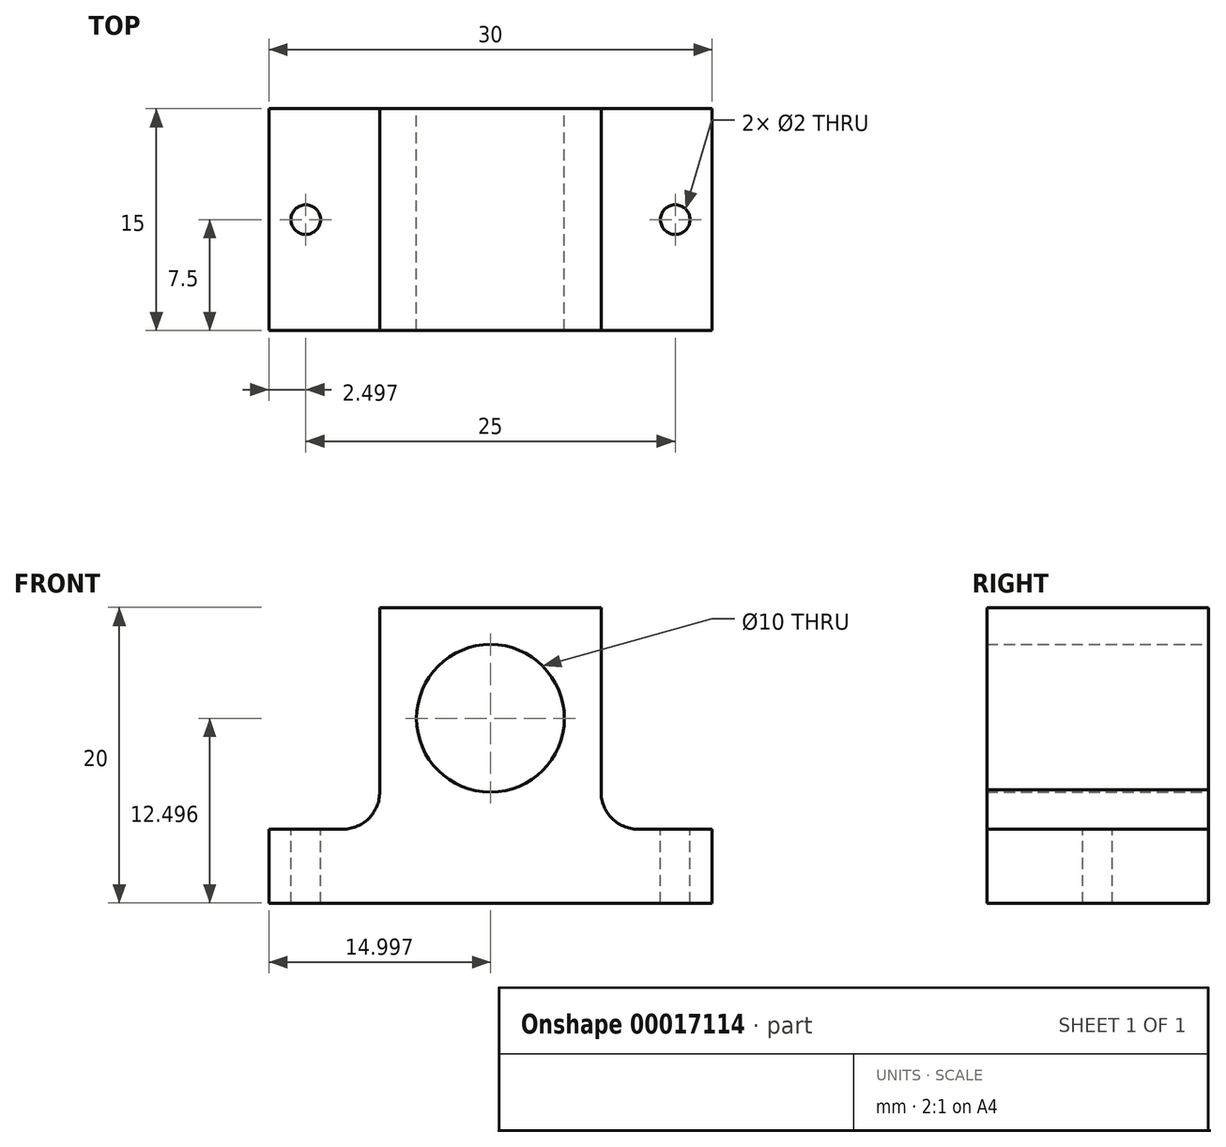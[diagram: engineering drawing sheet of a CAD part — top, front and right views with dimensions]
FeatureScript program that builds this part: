
annotation { "Feature Type Name" : "Feature", "Feature Type Description" : "" }
export const myFeature = defineFeature(function(context is Context, id is Id, definition is map)
    precondition{}
    {
        {
            var Q0;
            Q0=qCreatedBy(makeId("Front.planeOp"),FACE);
            var sketch = newSketch(context, id + "F0", { "sketchPlane" : qUnion([Q0])});
            skLineSegment(sketch, "E0.top", {"start": v(-46.25, -41.24) * mm, "end": v(-16.25, -41.24) * mm});
            skLineSegment(sketch, "E1", {"start": v(-46.25, -36.24) * mm, "end": v(-41.25, -36.24) * mm});
            skLineSegment(sketch, "E2", {"start": v(-16.27, -36.24) * mm, "end": v(-21.27, -36.24) * mm});
            skArc(sketch, "E3", {"start": v(-21.27, -36.24) * mm, "mid": v(-23.1, -35.45) * mm, "end": v(-23.76, -33.56) * mm});
            skArc(sketch, "E4", {"start": v(-41.25, -36.24) * mm, "mid": v(-39.42, -35.45) * mm, "end": v(-38.76, -33.56) * mm});
            skLineSegment(sketch, "E5", {"start": v(-38.76, -33.56) * mm, "end": v(-38.76, -21.24) * mm});
            skLineSegment(sketch, "E6", {"start": v(-38.76, -21.24) * mm, "end": v(-23.76, -21.24) * mm});
            skLineSegment(sketch, "E7", {"start": v(-23.76, -21.24) * mm, "end": v(-23.76, -33.56) * mm});
            skLineSegment(sketch, "E8", {"start": v(-46.25, -36.24) * mm, "end": v(-46.25, -41.24) * mm});
            skLineSegment(sketch, "E9", {"start": v(-16.27, -36.24) * mm, "end": v(-16.25, -41.24) * mm});
            skCircle(sketch, "E10", {"center": v(-31.25, -28.74) * mm, "radius": 5 * mm});
            skSolve(sketch);
        }
        {
            var Q0;
            Q0=makeQuery(id+"F0.imprint","IMPRINT",FACE,{"disambiguationData":[TD([[makeQuery(id+"F0.imprint","IMPRINT",EDGE,{"derivedFrom":sQuery(id+"F0.wireOp",EDGE,"E0.top")}),1.0]])]});
            extrude(context, id + "F1", {"entities" : qUnion([Q0]), "depth" : 15 * mm});
        }
        {
            var Q0;
            Q0=makeQuery(id+"F1.opExtrude","SWEPT_FACE",FACE,{"disambiguationData":[OSD([sQuery(id+"F0.wireOp",EDGE,"E1")])]});
            var sketch = newSketch(context, id + "F2", { "sketchPlane" : qUnion([Q0])});
            skCircle(sketch, "E11", {"center": v(-43.75, -7.5) * mm, "radius": 1 * mm});
            skSolve(sketch);
        }
        {
            var Q0;
            Q0=makeQuery(id+"F1.opExtrude","SWEPT_FACE",FACE,{"disambiguationData":[OSD([sQuery(id+"F0.wireOp",EDGE,"E2")])]});
            var sketch = newSketch(context, id + "F3", { "sketchPlane" : qUnion([Q0])});
            skCircle(sketch, "E12", {"center": v(-18.75, -7.5) * mm, "radius": 1 * mm});
            skSolve(sketch);
        }
        {
            var Q0;
            Q0=makeQuery(id+"F2.imprint","IMPRINT",FACE,{"disambiguationData":[TD([[makeQuery(id+"F2.imprint","IMPRINT",EDGE,{"derivedFrom":sQuery(id+"F2.wireOp",EDGE,"E11")}),1.0]])]});
            var Q1;
            Q1=makeQuery(id+"F3.imprint","IMPRINT",FACE,{"disambiguationData":[TD([[makeQuery(id+"F3.imprint","IMPRINT",EDGE,{"derivedFrom":sQuery(id+"F3.wireOp",EDGE,"E12")}),1.0]])]});
            extrude(context, id + "F4", {"entities" : qUnion([Q0, Q1]), "operationType" : NewBodyOperationType.REMOVE, "endBound" : BoundingType.THROUGH_ALL, "oppositeDirection" : true, "depth" : 25 * mm});
        }
    });
